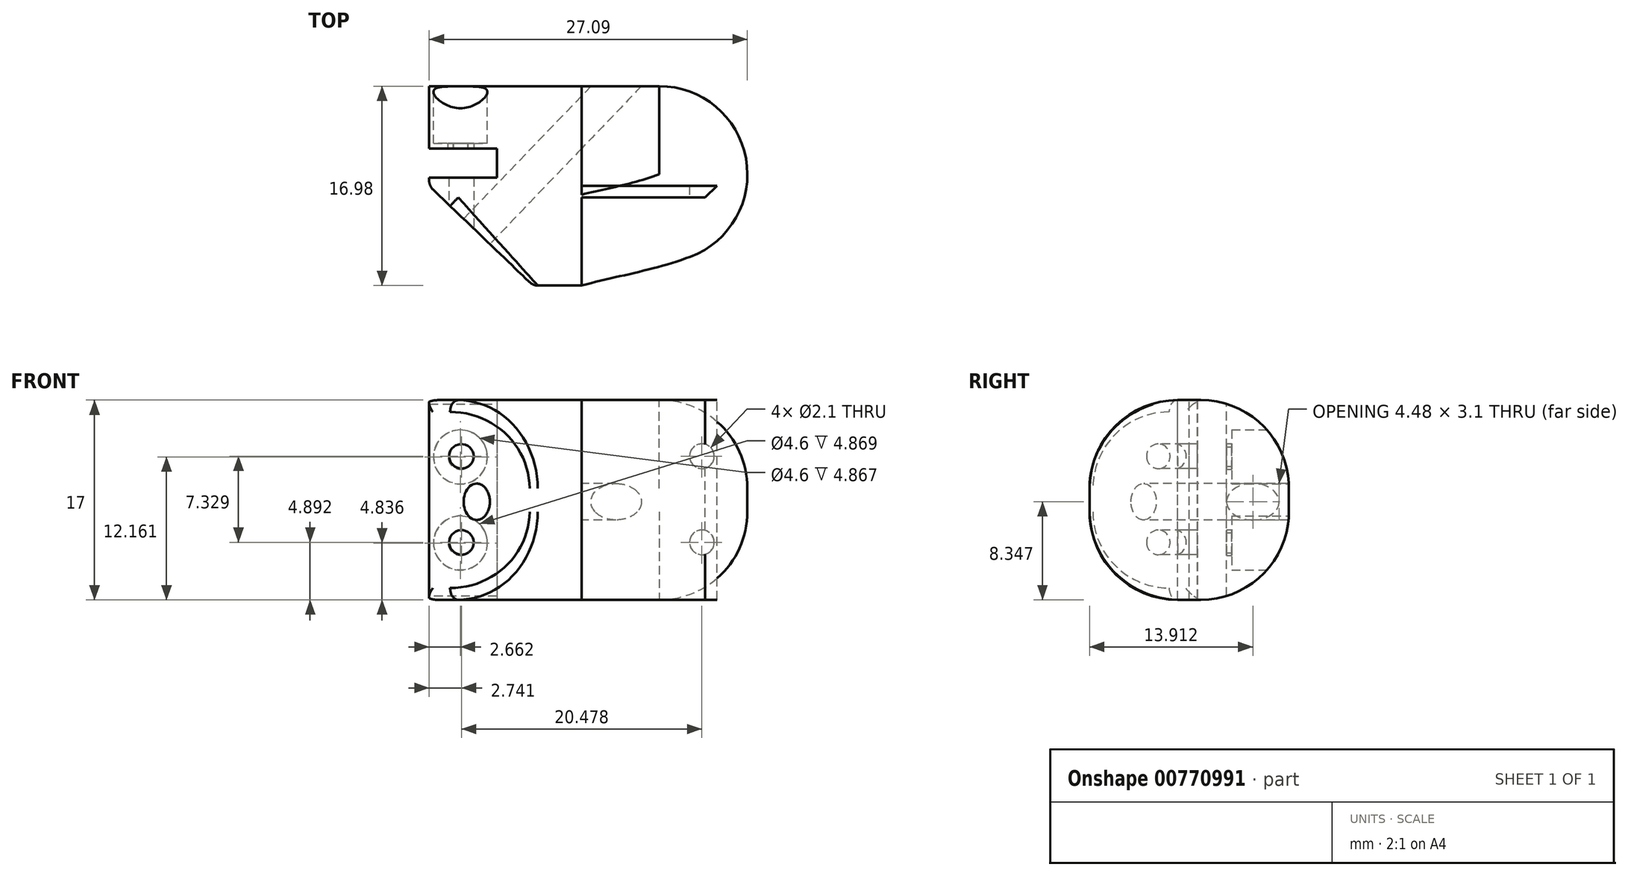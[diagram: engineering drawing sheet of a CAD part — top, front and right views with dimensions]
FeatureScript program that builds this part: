
annotation { "Feature Type Name" : "Feature", "Feature Type Description" : "" }
export const myFeature = defineFeature(function(context is Context, id is Id, definition is map)
    precondition{}
    {
        {
            var Q0;
            Q0=qCreatedBy(makeId("Top.planeOp"),FACE);
            var sketch = newSketch(context, id + "F0", { "sketchPlane" : qUnion([Q0])});
            skLineSegment(sketch, "E0.bottom", {"start": v(4.14, -8.48) * mm, "end": v(-4.14, -8.48) * mm});
            skLineSegment(sketch, "E0.top", {"start": v(12.98, 8.48) * mm, "end": v(-12.98, 8.48) * mm});
            skLineSegment(sketch, "E0.left", {"start": v(12.98, 0) * mm, "end": v(12.98, 8.48) * mm});
            skLineSegment(sketch, "E0.right", {"start": v(-12.98, 0) * mm, "end": v(-12.98, 8.48) * mm});
            skPoint(sketch, "E0.middle", {"position": v(0, 0) * mm});
            skLineSegment(sketch, "E1.top", {"start": v(-12.98, 8.48) * mm, "end": v(-4.14, 8.48) * mm});
            skLineSegment(sketch, "E2.top", {"start": v(12.98, 8.48) * mm, "end": v(4.14, 8.48) * mm});
            skLineSegment(sketch, "E3", {"start": v(-12.98, 0) * mm, "end": v(-4.14, -8.48) * mm});
            skLineSegment(sketch, "E4", {"start": v(4.14, -8.48) * mm, "end": v(12.98, 0) * mm});
            skPoint(sketch, "E5.orphan", {"position": v(12.98, -8.48) * mm});
            skPoint(sketch, "E6.orphan", {"position": v(-12.98, -8.48) * mm});
            skSolve(sketch);
        }
        {
            var Q0;
            Q0=makeQuery(id+"F0.imprint","IMPRINT",FACE,{"disambiguationData":[TD([[makeQuery(id+"F0.imprint","IMPRINT",EDGE,{"derivedFrom":sQuery(id+"F0.wireOp",EDGE,"E0.bottom")}),-1.0]])]});
            extrude(context, id + "F1", {"entities" : qUnion([Q0]), "depth" : 17 * mm, "offsetDistance" : 25 * mm});
        }
        {
            var Q0;
            Q0=makeQuery(id+"F1.opExtrude","CAP_EDGE",EDGE,{"disambiguationData":[OSD([sQuery(id+"F0.wireOp",EDGE,"E0.bottom")])],"isStart":false});
            var Q1;
            Q1=makeQuery(id+"F1.opExtrude","CAP_EDGE",EDGE,{"disambiguationData":[OSD([sQuery(id+"F0.wireOp",EDGE,"E0.bottom")])],"isStart":true});
            var Q2;
            Q2=makeQuery(id+"F1.opExtrude","CAP_EDGE",EDGE,{"disambiguationData":[OSD([sQuery(id+"F0.wireOp",EDGE,"E0.top"),sQuery(id+"F0.wireOp",EDGE,"E1.top"),sQuery(id+"F0.wireOp",EDGE,"E2.top")])],"isStart":false});
            var Q3;
            Q3=makeQuery(id+"F1.opExtrude","CAP_EDGE",EDGE,{"disambiguationData":[OSD([sQuery(id+"F0.wireOp",EDGE,"E0.top"),sQuery(id+"F0.wireOp",EDGE,"E1.top"),sQuery(id+"F0.wireOp",EDGE,"E2.top")])],"isStart":true});
            fillet(context, id + "F2", {"entities" : qUnion([Q0, Q1, Q2, Q3]), "radius" : 7.5 * mm, "tangentPropagation" : true, "allowEdgeOverflow" : false});
        }
        {
            var Q0;
            Q0=makeQuery(id+"F1.opExtrude","SWEPT_EDGE",EDGE,{"disambiguationData":[OSD([sQuery(id+"F0.wireOp",EDGE,"E0.right"),sQuery(id+"F0.wireOp",EDGE,"E3")])]});
            var Q1;
            Q1=makeQuery(id+"F2.opFillet","BLEND_EDGE",EDGE,{"blendedFrom":[makeQuery(id+"F1.opExtrude","CAP_EDGE",EDGE,{"disambiguationData":[OSD([sQuery(id+"F0.wireOp",EDGE,"E0.bottom")])],"isStart":true}),makeQuery(id+"F1.opExtrude","SWEPT_FACE",FACE,{"disambiguationData":[OSD([sQuery(id+"F0.wireOp",EDGE,"E3")])]})],"blendedInto":[makeQuery(id+"F1.opExtrude","SWEPT_FACE",FACE,{"disambiguationData":[OSD([sQuery(id+"F0.wireOp",EDGE,"E3")])]})]});
            var Q2;
            Q2=makeQuery(id+"F2.opFillet","BLEND_EDGE",EDGE,{"blendedFrom":[makeQuery(id+"F1.opExtrude","CAP_EDGE",EDGE,{"disambiguationData":[OSD([sQuery(id+"F0.wireOp",EDGE,"E0.bottom")])],"isStart":false}),makeQuery(id+"F1.opExtrude","SWEPT_FACE",FACE,{"disambiguationData":[OSD([sQuery(id+"F0.wireOp",EDGE,"E3")])]})],"blendedInto":[makeQuery(id+"F1.opExtrude","SWEPT_FACE",FACE,{"disambiguationData":[OSD([sQuery(id+"F0.wireOp",EDGE,"E3")])]})]});
            fillet(context, id + "F3", {"entities" : qUnion([Q0, Q1, Q2]), "radius" : 1 * mm, "allowEdgeOverflow" : false});
        }
        {
            var Q0;
            Q0=makeQuery(id+"F1.opExtrude","SWEPT_EDGE",EDGE,{"disambiguationData":[OSD([sQuery(id+"F0.wireOp",EDGE,"E0.bottom"),sQuery(id+"F0.wireOp",EDGE,"E4")])]});
            var Q1;
            Q1=makeQuery(id+"F2.opFillet","BLEND_EDGE",EDGE,{"blendedFrom":[makeQuery(id+"F1.opExtrude","CAP_EDGE",EDGE,{"disambiguationData":[OSD([sQuery(id+"F0.wireOp",EDGE,"E0.bottom")])],"isStart":true}),makeQuery(id+"F1.opExtrude","SWEPT_FACE",FACE,{"disambiguationData":[OSD([sQuery(id+"F0.wireOp",EDGE,"E4")])]})],"blendedInto":[makeQuery(id+"F1.opExtrude","SWEPT_FACE",FACE,{"disambiguationData":[OSD([sQuery(id+"F0.wireOp",EDGE,"E4")])]})]});
            fillet(context, id + "F4", {"entities" : qUnion([Q0, Q1]), "radius" : 1 * mm, "tangentPropagation" : true, "allowEdgeOverflow" : false});
        }
        {
            var Q0;
            Q0=makeQuery(id+"F1.opExtrude","SWEPT_FACE",FACE,{"disambiguationData":[OSD([sQuery(id+"F0.wireOp",EDGE,"E0.bottom")])]});
            var sketch = newSketch(context, id + "F5", { "sketchPlane" : qUnion([Q0])});
            skLineSegment(sketch, "E7.bottom", {"start": v(13, 0) * mm, "end": v(-13, 0) * mm});
            skLineSegment(sketch, "E7.top", {"start": v(13, 17.11) * mm, "end": v(-13, 17.11) * mm});
            skLineSegment(sketch, "E7.left", {"start": v(13, 0) * mm, "end": v(13, 17.11) * mm});
            skLineSegment(sketch, "E7.right", {"start": v(-13, 0) * mm, "end": v(-13, 17.11) * mm});
            skPoint(sketch, "E7.middle", {"position": v(0, 8.56) * mm});
            skPoint(sketch, "E8.top.end.orphan", {"position": v(10.24, 2.7) * mm});
            skPoint(sketch, "E8.bottom.end.orphan", {"position": v(10.24, 14.41) * mm});
            skPoint(sketch, "E8.left.end.orphan", {"position": v(-10.24, 2.7) * mm});
            skPoint(sketch, "E8.left.start.orphan", {"position": v(-10.24, 14.41) * mm});
            skLineSegment(sketch, "E9.bottom", {"start": v(-10.24, 12.22) * mm, "end": v(10.24, 12.22) * mm});
            skLineSegment(sketch, "E9.top", {"start": v(-10.24, 4.9) * mm, "end": v(10.24, 4.9) * mm});
            skLineSegment(sketch, "E9.left", {"start": v(-10.24, 12.22) * mm, "end": v(-10.24, 4.9) * mm});
            skLineSegment(sketch, "E9.right", {"start": v(10.24, 12.22) * mm, "end": v(10.24, 4.9) * mm});
            skLineSegment(sketch, "E10.bottom", {"start": v(10.24, 12.22) * mm, "end": v(-10.24, 12.22) * mm});
            skLineSegment(sketch, "E10.top", {"start": v(10.24, 4.9) * mm, "end": v(-10.24, 4.9) * mm});
            skSolve(sketch);
        }
        {
            var Q0;
            Q0=sQuery(id+"F5.wireOp",VERTEX,"E9.bottom.start");
            var Q1;
            Q1=sQuery(id+"F5.wireOp",VERTEX,"E9.top.start");
            var Q2;
            Q2=sQuery(id+"F5.wireOp",VERTEX,"E9.top.end");
            var Q3;
            Q3=sQuery(id+"F5.wireOp",VERTEX,"E9.bottom.end");
            var Q4;
            Q4=makeQuery(id+"FRGZ315mgqWVqYo_1.boolean.opBoolean","SPLIT",BODY,{"disambiguationData":[OD(0.0)],"derivedFrom":makeQuery(id+"F1.opExtrude","SWEPT_BODY",BODY,{"disambiguationData":[OSD([sQuery(id+"F0.wireOp",EDGE,"E0.bottom"),sQuery(id+"F0.wireOp",EDGE,"E0.top"),sQuery(id+"F0.wireOp",EDGE,"E0.left"),sQuery(id+"F0.wireOp",EDGE,"E0.right"),sQuery(id+"F0.wireOp",EDGE,"E1.top"),sQuery(id+"F0.wireOp",EDGE,"E2.top"),sQuery(id+"F0.wireOp",EDGE,"E3"),sQuery(id+"F0.wireOp",EDGE,"E4")])]})});
            var Q5;
            Q5=makeQuery(id+"FRGZ315mgqWVqYo_1.boolean.opBoolean","SPLIT",BODY,{"disambiguationData":[OD(1.0)],"derivedFrom":makeQuery(id+"F1.opExtrude","SWEPT_BODY",BODY,{"disambiguationData":[OSD([sQuery(id+"F0.wireOp",EDGE,"E0.bottom"),sQuery(id+"F0.wireOp",EDGE,"E0.top"),sQuery(id+"F0.wireOp",EDGE,"E0.left"),sQuery(id+"F0.wireOp",EDGE,"E0.right"),sQuery(id+"F0.wireOp",EDGE,"E1.top"),sQuery(id+"F0.wireOp",EDGE,"E2.top"),sQuery(id+"F0.wireOp",EDGE,"E3"),sQuery(id+"F0.wireOp",EDGE,"E4")])]})});
            hole(context, id + "F6", {"style" : HoleStyle.SIMPLE, "endStyle" : HoleEndStyle.BLIND, "holeDiameter" : 2.1 * mm, "majorDiameter" : 5 * mm, "holeDepth" : 12 * mm, "isTappedThrough" : true, "tappedDepth" : 12 * mm, "tapClearance" : 3, "locations" : qUnion([Q0, Q1, Q2, Q3]), "scope" : qUnion([Q4, Q5])});
        }
        {
            var Q0;
            Q0=makeQuery(id+"F1.opExtrude","SWEPT_FACE",FACE,{"disambiguationData":[OSD([sQuery(id+"F0.wireOp",EDGE,"E0.top"),sQuery(id+"F0.wireOp",EDGE,"E1.top"),sQuery(id+"F0.wireOp",EDGE,"E2.top")])]});
            var sketch = newSketch(context, id + "F7", { "sketchPlane" : qUnion([Q0])});
            skLineSegment(sketch, "E11.bottom", {"start": v(-10.19, 12.16) * mm, "end": v(10.32, 12.16) * mm});
            skLineSegment(sketch, "E11.top", {"start": v(-10.19, 4.84) * mm, "end": v(10.32, 4.84) * mm});
            skLineSegment(sketch, "E11.left", {"start": v(-10.19, 12.16) * mm, "end": v(-10.19, 4.84) * mm});
            skLineSegment(sketch, "E11.right", {"start": v(10.32, 12.16) * mm, "end": v(10.32, 4.84) * mm});
            skSolve(sketch);
        }
        {
            var Q0;
            Q0=sQuery(id+"F7.wireOp",VERTEX,"E11.top.start");
            var Q1;
            Q1=sQuery(id+"F7.wireOp",VERTEX,"E11.bottom.start");
            var Q2;
            Q2=sQuery(id+"F7.wireOp",VERTEX,"E11.bottom.end");
            var Q3;
            Q3=sQuery(id+"F7.wireOp",VERTEX,"E11.top.end");
            var Q4;
            Q4=makeQuery(id+"FRGZ315mgqWVqYo_1.boolean.opBoolean","SPLIT",BODY,{"disambiguationData":[OD(0.0)],"derivedFrom":makeQuery(id+"F1.opExtrude","SWEPT_BODY",BODY,{"disambiguationData":[OSD([sQuery(id+"F0.wireOp",EDGE,"E0.bottom"),sQuery(id+"F0.wireOp",EDGE,"E0.top"),sQuery(id+"F0.wireOp",EDGE,"E0.left"),sQuery(id+"F0.wireOp",EDGE,"E0.right"),sQuery(id+"F0.wireOp",EDGE,"E1.top"),sQuery(id+"F0.wireOp",EDGE,"E2.top"),sQuery(id+"F0.wireOp",EDGE,"E3"),sQuery(id+"F0.wireOp",EDGE,"E4")])]})});
            hole(context, id + "F8", {"style" : HoleStyle.C_BORE, "endStyle" : HoleEndStyle.BLIND, "holeDiameter" : 2.1 * mm, "cBoreDiameter" : 4.6 * mm, "cBoreDepth" : 3 * mm, "majorDiameter" : 5 * mm, "holeDepth" : 4 * mm, "isTappedThrough" : true, "tappedDepth" : 12 * mm, "tapClearance" : 3, "locations" : qUnion([Q0, Q1, Q2, Q3]), "scope" : qUnion([Q4])});
        }
        {
            var Q0;
            Q0=makeQuery(id+"F1.opExtrude","CAP_FACE",FACE,{"disambiguationData":[OSD([sQuery(id+"F0.wireOp",EDGE,"E0.bottom"),sQuery(id+"F0.wireOp",EDGE,"E0.top"),sQuery(id+"F0.wireOp",EDGE,"E0.left"),sQuery(id+"F0.wireOp",EDGE,"E0.right"),sQuery(id+"F0.wireOp",EDGE,"E1.top"),sQuery(id+"F0.wireOp",EDGE,"E2.top"),sQuery(id+"F0.wireOp",EDGE,"E3"),sQuery(id+"F0.wireOp",EDGE,"E4")])],"isStart":false});
            var sketch = newSketch(context, id + "F9", { "sketchPlane" : qUnion([Q0])});
            skLineSegment(sketch, "E12.bottom", {"start": v(0, 0) * mm, "end": v(13.17, 0) * mm});
            skLineSegment(sketch, "E12.top", {"start": v(0, 9.2) * mm, "end": v(13.17, 9.2) * mm});
            skLineSegment(sketch, "E12.left", {"start": v(0, 0) * mm, "end": v(0, 9.2) * mm});
            skLineSegment(sketch, "E12.right", {"start": v(13.17, 0) * mm, "end": v(13.17, 9.2) * mm});
            skLineSegment(sketch, "E13.bottom", {"start": v(0, 0) * mm, "end": v(13.18, 0) * mm});
            skLineSegment(sketch, "E13.top", {"start": v(0, -9.03) * mm, "end": v(13.18, -9.03) * mm});
            skLineSegment(sketch, "E13.left", {"start": v(0, 0) * mm, "end": v(0, -9.03) * mm});
            skLineSegment(sketch, "E13.right", {"start": v(13.18, 0) * mm, "end": v(13.18, -9.03) * mm});
            skSolve(sketch);
        }
        {
            var Q0;
            {var subQ1=sQuery(id+"F9.wireOp",EDGE,"E13.top");Q0=makeQuery(id+"F9.imprint","IMPRINT",FACE,{"disambiguationData":[TD([[makeQuery(id+"F9.imprint","IMPRINT",EDGE,{"derivedFrom":subQ1}),1.0]])]});}
            var Q1;
            {var subQ2=sQuery(id+"F9.wireOp",EDGE,"E12.top");Q1=makeQuery(id+"F9.imprint","IMPRINT",FACE,{"disambiguationData":[TD([[makeQuery(id+"F9.imprint","IMPRINT",EDGE,{"derivedFrom":subQ2}),-1.0]])]});}
            var Q2;
            {var subQ0=sQuery(id+"F9.wireOp",EDGE,"E13.left");var subQ1=sQuery(id+"F9.wireOp",EDGE,"E13.bottom");var subQ2=makeQuery(id+"F9.imprint","INTERSECT",VERTEX,{"derivedFrom":[sQuery(id+"F9.wireOp",EDGE,"E12.left"),subQ1,subQ0]});Q2=makeQuery(id+"F9.imprint","IMPRINT",FACE,{"disambiguationData":[TD([[makeQuery(id+"F9.imprint","IMPRINT",EDGE,{"disambiguationData":[TD([[subQ2,-1.0]])],"derivedFrom":subQ1}),-1.0]])]});}
            var Q3;
            {var subQ0=sQuery(id+"F9.wireOp",EDGE,"E13.bottom");var subQ1=sQuery(id+"F9.wireOp",EDGE,"E12.left");var subQ2=makeQuery(id+"F9.imprint","INTERSECT",VERTEX,{"derivedFrom":[subQ1,subQ0,sQuery(id+"F9.wireOp",EDGE,"E13.left")]});Q3=makeQuery(id+"F9.imprint","IMPRINT",FACE,{"disambiguationData":[TD([[makeQuery(id+"F9.imprint","IMPRINT",EDGE,{"disambiguationData":[TD([[subQ2,-1.0]])],"derivedFrom":subQ1}),-1.0]])]});}
            extrude(context, id + "F10", {"entities" : qUnion([Q0, Q1, Q2, Q3]), "operationType" : NewBodyOperationType.REMOVE, "endBound" : BoundingType.THROUGH_ALL, "oppositeDirection" : true, "depth" : 17.3 * mm, "offsetDistance" : 25 * mm});
        }
        {
            var Q0;
            Q0=qCreatedBy(makeId("Top.planeOp"),FACE);
            var sketch = newSketch(context, id + "F11", { "sketchPlane" : qUnion([Q0])});
            skPoint(sketch, "E14.start.orphan", {"position": v(0, 8.49) * mm});
            skLineSegment(sketch, "E15", {"start": v(0, 8.49) * mm, "end": v(12.42, 8.49) * mm});
            skFitSpline(sketch, "E16", {"points": [v(0, -8.49) * mm, v(7.15, -6.72) * mm, v(14.8, -2.26) * mm, v(17.71, 6.1) * mm, v(18, 8.49) * mm], "startDerivative": vector(28.15, 7.64) * mm, "endDerivative": vector(-0.6, 11.55) * mm});
            skFitSpline(sketch, "E17", {"points": [v(17.95, 7.58) * mm, v(16.45, 7.9) * mm, v(12.42, 8.49) * mm], "startDerivative": vector(-3.46, 0.82) * mm, "endDerivative": vector(-7.3, 0.97) * mm});
            skLineSegment(sketch, "E18", {"start": v(0, 8.49) * mm, "end": v(0, -8.49) * mm});
            skSolve(sketch);
        }
        {
            var Q0;
            Q0=makeQuery(id+"F11.imprint","IMPRINT",FACE,{"disambiguationData":[TD([[makeQuery(id+"F11.imprint","IMPRINT",EDGE,{"derivedFrom":sQuery(id+"F11.wireOp",EDGE,"E15")}),-1.0]])]});
            extrude(context, id + "F12", {"entities" : qUnion([Q0]), "depth" : 17 * mm, "offsetDistance" : 25 * mm});
        }
        {
            var Q0;
            Q0=makeQuery(id+"F12.opExtrude","CAP_EDGE",EDGE,{"disambiguationData":[OSD([sQuery(id+"F11.wireOp",EDGE,"E15")])],"isStart":false});
            var Q1;
            Q1=makeQuery(id+"F12.opExtrude","CAP_EDGE",EDGE,{"disambiguationData":[OSD([sQuery(id+"F11.wireOp",EDGE,"E15")])],"isStart":true});
            fillet(context, id + "F13", {"entities" : qUnion([Q0, Q1]), "radius" : 7.5 * mm, "tangentPropagation" : true, "allowEdgeOverflow" : false});
        }
        {
            var Q0;
            Q0=makeQuery(id+"F12.opExtrude","CAP_EDGE",EDGE,{"disambiguationData":[OSD([sQuery(id+"F11.wireOp",EDGE,"E16")])],"isStart":false});
            var Q1;
            Q1=makeQuery(id+"F12.opExtrude","CAP_EDGE",EDGE,{"disambiguationData":[OSD([sQuery(id+"F11.wireOp",EDGE,"E16")])],"isStart":true});
            fillet(context, id + "F14", {"entities" : qUnion([Q0, Q1]), "radius" : 7.5 * mm, "tangentPropagation" : true, "allowEdgeOverflow" : false});
        }
        {
            var Q0;
            Q0=makeQuery(id+"F1.opExtrude","SWEPT_FACE",FACE,{"disambiguationData":[OSD([sQuery(id+"F0.wireOp",EDGE,"E3")])]});
            var sketch = newSketch(context, id + "F15", { "sketchPlane" : qUnion([Q0])});
            skPoint(sketch, "E19", {"position": v(-3.75, 8.35) * mm});
            skCircle(sketch, "E20", {"center": v(-3.75, 8.35) * mm, "radius": 1.55 * mm});
            skSolve(sketch);
        }
        {
            var Q0;
            Q0=makeQuery(id+"F15.imprint","IMPRINT",FACE,{"disambiguationData":[TD([[makeQuery(id+"F15.imprint","IMPRINT",EDGE,{"derivedFrom":sQuery(id+"F15.wireOp",EDGE,"E20")}),1.0]])]});
            extrude(context, id + "F16", {"entities" : qUnion([Q0]), "operationType" : NewBodyOperationType.REMOVE, "endBound" : BoundingType.THROUGH_ALL, "oppositeDirection" : true, "depth" : 25 * mm, "offsetDistance" : 25 * mm});
        }
        {
            var Q0;
            Q0=qCreatedBy(makeId("Top.planeOp"),FACE);
            var sketch = newSketch(context, id + "F17", { "sketchPlane" : qUnion([Q0])});
            skLineSegment(sketch, "E21.bottom", {"start": v(-7.22, 0.7) * mm, "end": v(-13, 0.7) * mm});
            skLineSegment(sketch, "E21.top", {"start": v(-7.22, 3.18) * mm, "end": v(-13, 3.18) * mm});
            skLineSegment(sketch, "E21.left", {"start": v(-7.22, 0.7) * mm, "end": v(-7.22, 3.18) * mm});
            skLineSegment(sketch, "E21.right", {"start": v(-13, 0.7) * mm, "end": v(-13, 3.18) * mm});
            skSolve(sketch);
        }
        {
            var Q0;
            Q0 = qSketchRegion(id + "F17", true);
            extrude(context, id + "F18", {"entities" : qUnion([Q0]), "operationType" : NewBodyOperationType.REMOVE, "oppositeDirection" : true, "depth" : -18 * mm, "offsetDistance" : 25 * mm});
        }
    });
